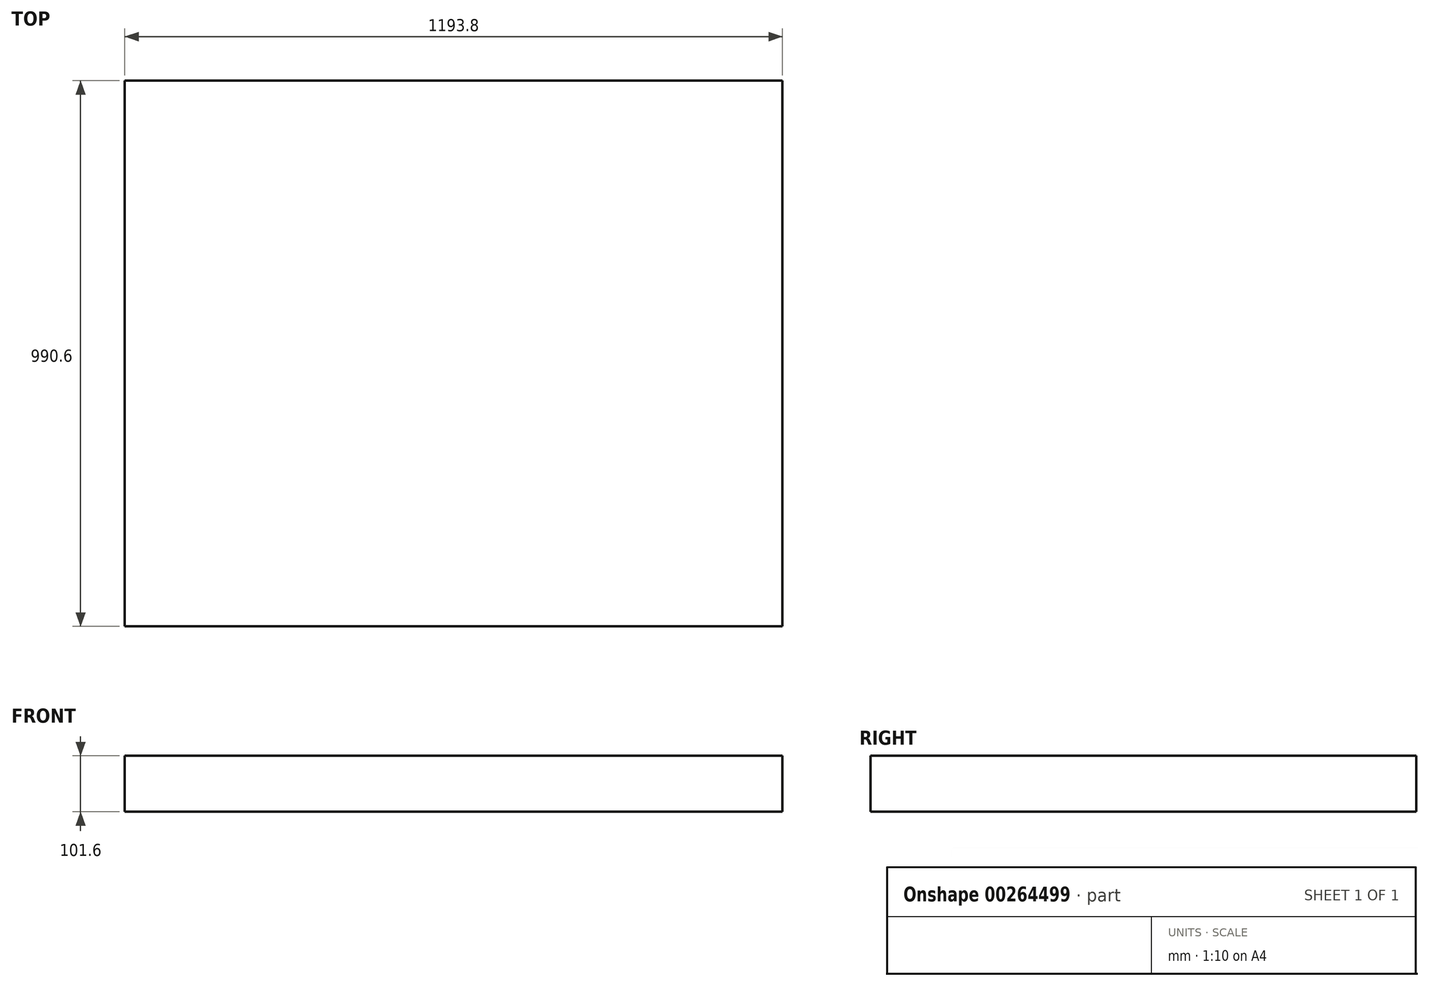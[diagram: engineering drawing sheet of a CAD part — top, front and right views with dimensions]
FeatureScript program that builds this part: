
annotation { "Feature Type Name" : "Feature", "Feature Type Description" : "" }
export const myFeature = defineFeature(function(context is Context, id is Id, definition is map)
    precondition{}
    {
        {
            var Q0;
            Q0=qCreatedBy(makeId("Top.planeOp"),FACE);
            var sketch = newSketch(context, id + "F0", { "sketchPlane" : qUnion([Q0])});
            skLineSegment(sketch, "E0.bottom", {"start": v(-596.9, 495.3) * mm, "end": v(596.9, 495.3) * mm});
            skLineSegment(sketch, "E0.top", {"start": v(-596.9, -495.3) * mm, "end": v(596.9, -495.3) * mm});
            skLineSegment(sketch, "E0.left", {"start": v(-596.9, 495.3) * mm, "end": v(-596.9, -495.3) * mm});
            skLineSegment(sketch, "E0.right", {"start": v(596.9, 495.3) * mm, "end": v(596.9, -495.3) * mm});
            skLineSegment(sketch, "E1", {"start": v(0, 0) * mm, "end": v(0, -495.3) * mm, "construction": true});
            skLineSegment(sketch, "E2", {"start": v(0, 0) * mm, "end": v(-596.9, 0) * mm, "construction": true});
            skSolve(sketch);
        }
        {
            var Q0;
            Q0 = qSketchRegion(id + "F0", true);
            extrude(context, id + "F1", {"entities" : qUnion([Q0]), "depth" : 101.6 * mm});
        }
    });
